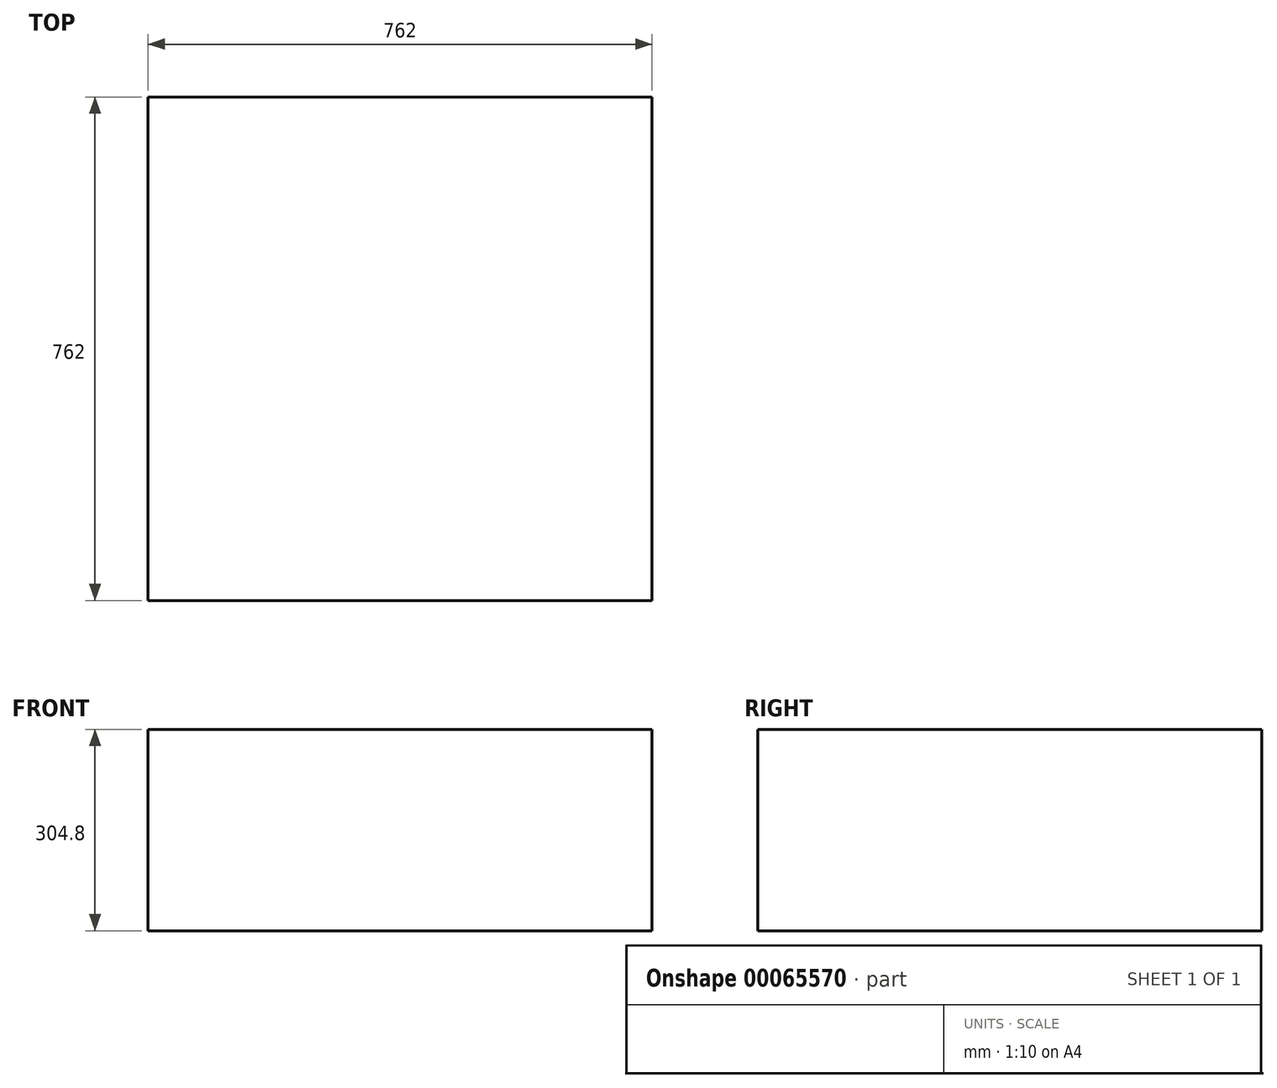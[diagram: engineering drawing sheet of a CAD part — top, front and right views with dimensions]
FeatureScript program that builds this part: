
annotation { "Feature Type Name" : "Feature", "Feature Type Description" : "" }
export const myFeature = defineFeature(function(context is Context, id is Id, definition is map)
    precondition{}
    {
        {
            var Q0;
            Q0=qCreatedBy(makeId("Top.planeOp"),FACE);
            var sketch = newSketch(context, id + "F0", { "sketchPlane" : qUnion([Q0])});
            skLineSegment(sketch, "E0.bottom", {"start": v(0, 0) * mm, "end": v(762, 0) * mm});
            skLineSegment(sketch, "E0.top", {"start": v(0, -762) * mm, "end": v(762, -762) * mm});
            skLineSegment(sketch, "E0.left", {"start": v(0, 0) * mm, "end": v(0, -762) * mm});
            skLineSegment(sketch, "E0.right", {"start": v(762, 0) * mm, "end": v(762, -762) * mm});
            skSolve(sketch);
        }
        {
            var Q0;
            Q0 = qSketchRegion(id + "F0", true);
            extrude(context, id + "F1", {"entities" : qUnion([Q0]), "depth" : 304.8 * mm});
        }
    });
